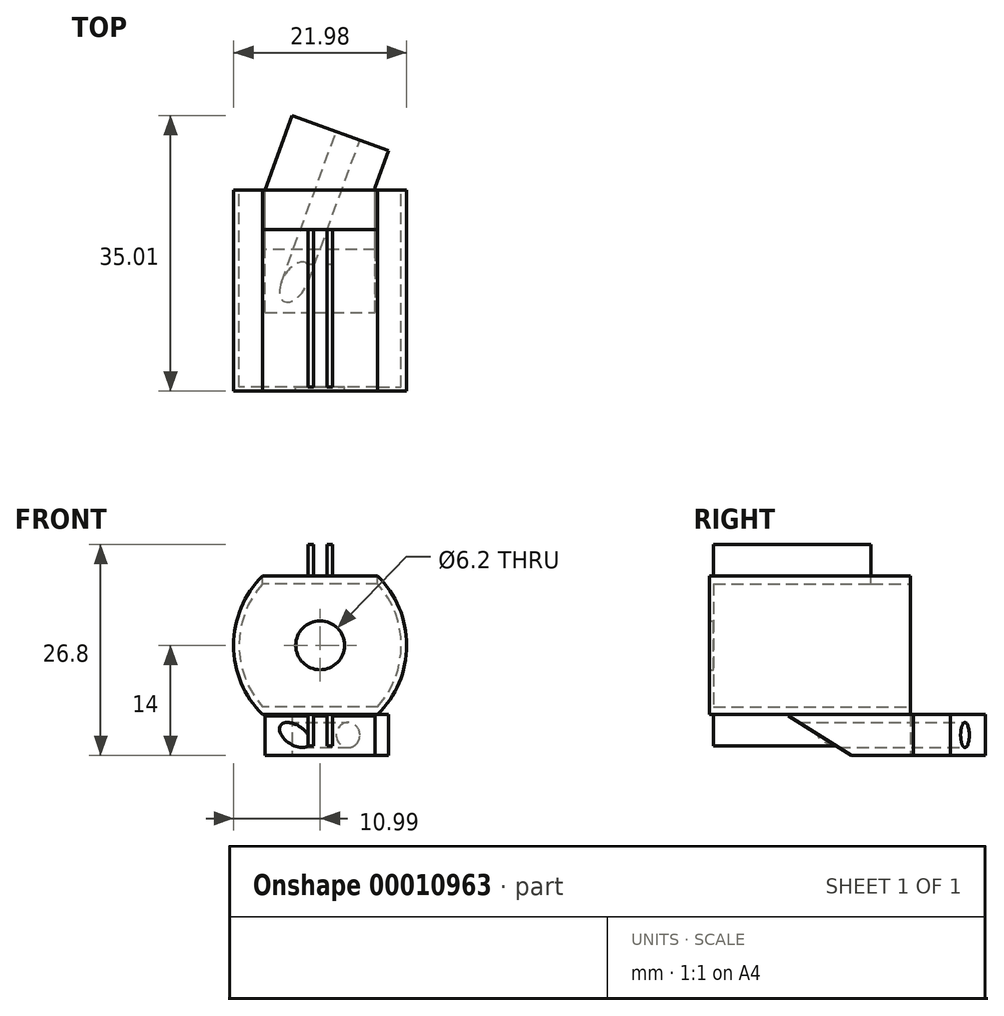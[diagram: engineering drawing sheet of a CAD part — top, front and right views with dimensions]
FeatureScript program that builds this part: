
annotation { "Feature Type Name" : "Feature", "Feature Type Description" : "" }
export const myFeature = defineFeature(function(context is Context, id is Id, definition is map)
    precondition{}
    {
        {
            var Q0;
            Q0=qCreatedBy(makeId("Front.planeOp"),FACE);
            var sketch = newSketch(context, id + "F0", { "sketchPlane" : qUnion([Q0])});
            skLineSegment(sketch, "E0.bottom", {"start": v(8.64, -7.8) * mm, "end": v(-5.96, -7.8) * mm});
            skLineSegment(sketch, "E0.top", {"start": v(8.64, 7.8) * mm, "end": v(-5.96, 7.8) * mm});
            skLineSegment(sketch, "E0.left", {"start": v(8.64, -7.8) * mm, "end": v(8.64, 7.8) * mm, "construction": true});
            skLineSegment(sketch, "E0.right", {"start": v(-5.96, -7.8) * mm, "end": v(-5.96, 7.8) * mm, "construction": true});
            skLineSegment(sketch, "E1", {"start": v(-5.96, 0) * mm, "end": v(8.64, 0) * mm, "construction": true});
            skArc(sketch, "E2", {"start": v(-5.96, 7.8) * mm, "mid": v(-8.96, 0) * mm, "end": v(-5.96, -7.8) * mm});
            skArc(sketch, "E3", {"start": v(8.64, -7.8) * mm, "mid": v(11.64, 0) * mm, "end": v(8.64, 7.8) * mm});
            skLineSegment(sketch, "E4.bottom", {"start": v(-8.96, 8.8) * mm, "end": v(11.64, 8.8) * mm, "construction": true});
            skLineSegment(sketch, "E4.top", {"start": v(-8.96, -8.8) * mm, "end": v(11.64, -8.8) * mm, "construction": true});
            skLineSegment(sketch, "E4.left", {"start": v(-8.96, 8.8) * mm, "end": v(-8.96, -8.8) * mm, "construction": true});
            skLineSegment(sketch, "E4.right", {"start": v(11.64, 8.8) * mm, "end": v(11.64, -8.8) * mm, "construction": true});
            skLineSegment(sketch, "E5", {"start": v(-5.96, 0) * mm, "end": v(-8.96, 0) * mm, "construction": true});
            skLineSegment(sketch, "E6", {"start": v(8.64, 0) * mm, "end": v(11.64, 0) * mm, "construction": true});
            skLineSegment(sketch, "E7", {"start": v(1.34, 7.8) * mm, "end": v(1.34, 8.8) * mm, "construction": true});
            skLineSegment(sketch, "E8", {"start": v(1.34, -7.8) * mm, "end": v(1.34, -8.8) * mm, "construction": true});
            skLineSegment(sketch, "E9", {"start": v(-5.96, 8.8) * mm, "end": v(-8.96, 8.8) * mm, "construction": true});
            skLineSegment(sketch, "E10", {"start": v(-8.96, -8.8) * mm, "end": v(-5.96, -8.8) * mm, "construction": true});
            skLineSegment(sketch, "E11", {"start": v(8.64, 8.8) * mm, "end": v(11.64, 8.8) * mm, "construction": true});
            skLineSegment(sketch, "E12", {"start": v(11.64, -8.8) * mm, "end": v(8.64, -8.8) * mm, "construction": true});
            skArc(sketch, "E13", {"start": v(-5.96, 8.8) * mm, "mid": v(-9.65, 0) * mm, "end": v(-5.96, -8.8) * mm});
            skArc(sketch, "E14", {"start": v(8.64, -8.8) * mm, "mid": v(12.33, 0) * mm, "end": v(8.64, 8.8) * mm});
            skLineSegment(sketch, "E15", {"start": v(-5.96, 8.8) * mm, "end": v(-0.2, 8.8) * mm});
            skLineSegment(sketch, "E16", {"start": v(-5.96, -8.8) * mm, "end": v(8.64, -8.8) * mm});
            skLineSegment(sketch, "E17.bottom", {"start": v(2.9, 12.8) * mm, "end": v(2.2, 12.8) * mm});
            skLineSegment(sketch, "E17.top", {"start": v(2.9, 8.8) * mm, "end": v(2.2, 8.8) * mm, "construction": true});
            skLineSegment(sketch, "E17.left", {"start": v(2.9, 12.8) * mm, "end": v(2.9, 8.8) * mm});
            skLineSegment(sketch, "E17.right", {"start": v(2.2, 12.8) * mm, "end": v(2.2, 8.8) * mm});
            skLineSegment(sketch, "E18.bottom", {"start": v(0.5, 12.8) * mm, "end": v(-0.2, 12.8) * mm});
            skLineSegment(sketch, "E18.top", {"start": v(0.5, 8.8) * mm, "end": v(-0.2, 8.8) * mm, "construction": true});
            skLineSegment(sketch, "E18.left", {"start": v(0.5, 12.8) * mm, "end": v(0.5, 8.8) * mm});
            skLineSegment(sketch, "E18.right", {"start": v(-0.2, 12.8) * mm, "end": v(-0.2, 8.8) * mm});
            skLineSegment(sketch, "E19", {"start": v(0.5, 10.8) * mm, "end": v(2.2, 10.8) * mm, "construction": true});
            skPoint(sketch, "E19.endSnap0", {"position": v(2.2, 10.8) * mm});
            skLineSegment(sketch, "E20", {"start": v(1.34, 10.8) * mm, "end": v(1.34, 8.8) * mm, "construction": true});
            skLineSegment(sketch, "E21.trimOffspring", {"start": v(0.5, 8.8) * mm, "end": v(2.2, 8.8) * mm});
            skLineSegment(sketch, "E22.trimOffspring", {"start": v(2.9, 8.8) * mm, "end": v(8.64, 8.8) * mm});
            skLineSegment(sketch, "E23.MirrorCS", {"start": v(2.9, -12.8) * mm, "end": v(2.2, -12.8) * mm});
            skLineSegment(sketch, "E24.MirrorCS", {"start": v(2.2, -12.8) * mm, "end": v(2.2, -8.8) * mm});
            skLineSegment(sketch, "E25.MirrorCS", {"start": v(0.5, -12.8) * mm, "end": v(-0.2, -12.8) * mm});
            skLineSegment(sketch, "E26.MirrorCS", {"start": v(0.5, -12.8) * mm, "end": v(0.5, -8.8) * mm});
            skLineSegment(sketch, "E27.MirrorCS", {"start": v(1.34, -10.8) * mm, "end": v(1.34, -8.8) * mm, "construction": true});
            skLineSegment(sketch, "E28.MirrorCS", {"start": v(-0.2, -12.8) * mm, "end": v(-0.2, -8.8) * mm});
            skLineSegment(sketch, "E29.MirrorCS", {"start": v(0.5, -10.8) * mm, "end": v(2.2, -10.8) * mm, "construction": true});
            skPoint(sketch, "E30.MirrorP", {"position": v(2.2, -10.8) * mm});
            skLineSegment(sketch, "E31.MirrorCS", {"start": v(2.9, -12.8) * mm, "end": v(2.9, -8.8) * mm});
            skSolve(sketch);
        }
        {
            var Q0;
            Q0 = qSketchRegion(id + "F0", true);
            extrude(context, id + "F1", {"entities" : qUnion([Q0]), "depth" : 25 * mm});
        }
        {
            var Q0;
            Q0=makeQuery(id+"F1.opExtrude","CAP_FACE",FACE,{"disambiguationData":[OSD([sQuery(id+"F0.wireOp",EDGE,"E0.bottom"),sQuery(id+"F0.wireOp",EDGE,"E0.top"),sQuery(id+"F0.wireOp",EDGE,"E2"),sQuery(id+"F0.wireOp",EDGE,"E3"),sQuery(id+"F0.wireOp",EDGE,"E13"),sQuery(id+"F0.wireOp",EDGE,"E14"),sQuery(id+"F0.wireOp",EDGE,"E15"),sQuery(id+"F0.wireOp",EDGE,"E16"),sQuery(id+"F0.wireOp",EDGE,"b434bd08-9800-4ba8-86db-d2efdbc153f3.bottom"),sQuery(id+"F0.wireOp",EDGE,"b434bd08-9800-4ba8-86db-d2efdbc153f3.top"),sQuery(id+"F0.wireOp",EDGE,"b434bd08-9800-4ba8-86db-d2efdbc153f3.left"),sQuery(id+"F0.wireOp",EDGE,"b434bd08-9800-4ba8-86db-d2efdbc153f3.right"),sQuery(id+"F0.wireOp",EDGE,"e7ebadcb-095e-4845-b03f-53081afac3a3.left"),sQuery(id+"F0.wireOp",EDGE,"e7ebadcb-095e-4845-b03f-53081afac3a3.right"),sQuery(id+"F0.wireOp",EDGE,"705c6145-6b34-48c9-8387-370b78359147.trimOffspring"),sQuery(id+"F0.wireOp",EDGE,"64f156d2-0356-4655-a443-7f1b8c19d74f0.MirrorCS"),sQuery(id+"F0.wireOp",EDGE,"0e9b9350-3440-4c2f-b366-a9727cc7379a0.MirrorCS"),sQuery(id+"F0.wireOp",EDGE,"648d7584-0f17-4bc0-a4b6-e825e98bb7620.MirrorCS"),sQuery(id+"F0.wireOp",EDGE,"4065b29f-1cc0-427a-abbd-1765cdf15fe30.MirrorCS"),sQuery(id+"F0.wireOp",EDGE,"a082fcf7-8d46-4496-8694-aedf1b6aa8e40.MirrorCS"),sQuery(id+"F0.wireOp",EDGE,"b75a4674-45b7-4ab3-ad6c-8b33a67d18960.MirrorCS")])],"isStart":true});
            var sketch = newSketch(context, id + "F2", { "sketchPlane" : qUnion([Q0])});
            skLineSegment(sketch, "E32.bottom", {"start": v(5.96, 7.8) * mm, "end": v(-8.64, 7.8) * mm});
            skLineSegment(sketch, "E32.top", {"start": v(5.96, 18.17) * mm, "end": v(-8.64, 18.17) * mm});
            skLineSegment(sketch, "E32.left", {"start": v(5.96, 7.8) * mm, "end": v(5.96, 18.17) * mm});
            skLineSegment(sketch, "E32.right", {"start": v(-8.64, 7.8) * mm, "end": v(-8.64, 18.17) * mm});
            skSolve(sketch);
        }
        {
            var Q0;
            Q0 = qSketchRegion(id + "F2", true);
            extrude(context, id + "F3", {"entities" : qUnion([Q0]), "operationType" : NewBodyOperationType.REMOVE, "oppositeDirection" : true, "depth" : 5 * mm});
        }
        {
            var Q0;
            Q0=makeQuery(id+"F1.opExtrude","CAP_FACE",FACE,{"disambiguationData":[OSD([sQuery(id+"F0.wireOp",EDGE,"E0.bottom"),sQuery(id+"F0.wireOp",EDGE,"E0.top"),sQuery(id+"F0.wireOp",EDGE,"E2"),sQuery(id+"F0.wireOp",EDGE,"E3"),sQuery(id+"F0.wireOp",EDGE,"E13"),sQuery(id+"F0.wireOp",EDGE,"E14"),sQuery(id+"F0.wireOp",EDGE,"E15"),sQuery(id+"F0.wireOp",EDGE,"E16"),sQuery(id+"F0.wireOp",EDGE,"b434bd08-9800-4ba8-86db-d2efdbc153f3.bottom"),sQuery(id+"F0.wireOp",EDGE,"b434bd08-9800-4ba8-86db-d2efdbc153f3.top"),sQuery(id+"F0.wireOp",EDGE,"b434bd08-9800-4ba8-86db-d2efdbc153f3.left"),sQuery(id+"F0.wireOp",EDGE,"b434bd08-9800-4ba8-86db-d2efdbc153f3.right"),sQuery(id+"F0.wireOp",EDGE,"e7ebadcb-095e-4845-b03f-53081afac3a3.left"),sQuery(id+"F0.wireOp",EDGE,"e7ebadcb-095e-4845-b03f-53081afac3a3.right"),sQuery(id+"F0.wireOp",EDGE,"705c6145-6b34-48c9-8387-370b78359147.trimOffspring"),sQuery(id+"F0.wireOp",EDGE,"64f156d2-0356-4655-a443-7f1b8c19d74f0.MirrorCS"),sQuery(id+"F0.wireOp",EDGE,"0e9b9350-3440-4c2f-b366-a9727cc7379a0.MirrorCS"),sQuery(id+"F0.wireOp",EDGE,"648d7584-0f17-4bc0-a4b6-e825e98bb7620.MirrorCS"),sQuery(id+"F0.wireOp",EDGE,"4065b29f-1cc0-427a-abbd-1765cdf15fe30.MirrorCS"),sQuery(id+"F0.wireOp",EDGE,"a082fcf7-8d46-4496-8694-aedf1b6aa8e40.MirrorCS"),sQuery(id+"F0.wireOp",EDGE,"b75a4674-45b7-4ab3-ad6c-8b33a67d18960.MirrorCS")])],"isStart":false});
            var sketch = newSketch(context, id + "F4", { "sketchPlane" : qUnion([Q0])});
            skArc(sketch, "E33.0", {"start": v(-5.96, 8.8) * mm, "mid": v(-9.65, 0) * mm, "end": v(-5.96, -8.8) * mm});
            skArc(sketch, "E34.0", {"start": v(8.64, -8.8) * mm, "mid": v(12.33, 0) * mm, "end": v(8.64, 8.8) * mm});
            skLineSegment(sketch, "E35", {"start": v(-5.96, 8.8) * mm, "end": v(8.64, 8.8) * mm});
            skLineSegment(sketch, "E36", {"start": v(8.64, -8.8) * mm, "end": v(-5.96, -8.8) * mm});
            skLineSegment(sketch, "E37", {"start": v(1.34, 8.8) * mm, "end": v(1.34, 0) * mm, "construction": true});
            skLineSegment(sketch, "E38", {"start": v(1.34, 0) * mm, "end": v(1.34, -8.8) * mm, "construction": true});
            skCircle(sketch, "E39", {"center": v(1.34, 0) * mm, "radius": 3.1 * mm});
            skSolve(sketch);
        }
        {
            var Q0;
            Q0 = qSketchRegion(id + "F4", true);
            extrude(context, id + "F5", {"entities" : qUnion([Q0]), "operationType" : NewBodyOperationType.ADD, "depth" : 0.5 * mm});
        }
        {
            var Q0;
            Q0=qCreatedBy(makeId("Top.planeOp"),FACE);
            cPlane(context, id + "F6", {"entities" : qUnion([Q0]), "cplaneType" : CPlaneType.OFFSET, "offset" : 14 * mm, "oppositeDirection" : true, "width" : 150 * mm, "height" : 150 * mm});
        }
        {
            var Q0;
            Q0=qCreatedBy(id+"F6.planeOp",FACE);
            var sketch = newSketch(context, id + "F7", { "sketchPlane" : qUnion([Q0])});
            skLineSegment(sketch, "E40.bottom", {"start": v(-5.66, -15.5) * mm, "end": v(8.34, -15.5) * mm});
            skLineSegment(sketch, "E40.top", {"start": v(-5.66, 0) * mm, "end": v(8.34, 0) * mm});
            skLineSegment(sketch, "E40.left", {"start": v(-5.66, -15.5) * mm, "end": v(-5.66, 0) * mm});
            skLineSegment(sketch, "E40.right", {"start": v(8.34, -15.5) * mm, "end": v(8.34, 0) * mm});
            skLineSegment(sketch, "E41", {"start": v(0.5, -25) * mm, "end": v(2.2, -25) * mm, "construction": true});
            skLineSegment(sketch, "E42", {"start": v(1.34, -25) * mm, "end": v(1.34, -15.5) * mm, "construction": true});
            skSolve(sketch);
        }
        {
            var Q0;
            Q0 = qSketchRegion(id + "F7", true);
            var Q1;
            Q1=makeQuery(id+"F1.opExtrude","SWEPT_BODY",BODY,{"disambiguationData":[OSD([sQuery(id+"F0.wireOp",EDGE,"E0.bottom"),sQuery(id+"F0.wireOp",EDGE,"E0.top"),sQuery(id+"F0.wireOp",EDGE,"E2"),sQuery(id+"F0.wireOp",EDGE,"E3"),sQuery(id+"F0.wireOp",EDGE,"E13"),sQuery(id+"F0.wireOp",EDGE,"E14"),sQuery(id+"F0.wireOp",EDGE,"E15"),sQuery(id+"F0.wireOp",EDGE,"E16"),sQuery(id+"F0.wireOp",EDGE,"b434bd08-9800-4ba8-86db-d2efdbc153f3.bottom"),sQuery(id+"F0.wireOp",EDGE,"b434bd08-9800-4ba8-86db-d2efdbc153f3.top"),sQuery(id+"F0.wireOp",EDGE,"b434bd08-9800-4ba8-86db-d2efdbc153f3.left"),sQuery(id+"F0.wireOp",EDGE,"b434bd08-9800-4ba8-86db-d2efdbc153f3.right"),sQuery(id+"F0.wireOp",EDGE,"e7ebadcb-095e-4845-b03f-53081afac3a3.left"),sQuery(id+"F0.wireOp",EDGE,"e7ebadcb-095e-4845-b03f-53081afac3a3.right"),sQuery(id+"F0.wireOp",EDGE,"705c6145-6b34-48c9-8387-370b78359147.trimOffspring"),sQuery(id+"F0.wireOp",EDGE,"64f156d2-0356-4655-a443-7f1b8c19d74f0.MirrorCS"),sQuery(id+"F0.wireOp",EDGE,"0e9b9350-3440-4c2f-b366-a9727cc7379a0.MirrorCS"),sQuery(id+"F0.wireOp",EDGE,"648d7584-0f17-4bc0-a4b6-e825e98bb7620.MirrorCS"),sQuery(id+"F0.wireOp",EDGE,"4065b29f-1cc0-427a-abbd-1765cdf15fe30.MirrorCS"),sQuery(id+"F0.wireOp",EDGE,"a082fcf7-8d46-4496-8694-aedf1b6aa8e40.MirrorCS"),sQuery(id+"F0.wireOp",EDGE,"b75a4674-45b7-4ab3-ad6c-8b33a67d18960.MirrorCS")])]});
            extrude(context, id + "F8", {"entities" : qUnion([Q0]), "operationType" : NewBodyOperationType.ADD, "endBound" : BoundingType.UP_TO_BODY, "endBoundEntityBody" : qUnion([Q1]), "depth" : 25 * mm});
        }
        {
            var Q0;
            Q0=makeQuery(id+"F8.opExtrude","CAP_FACE",FACE,{"disambiguationData":[OSD([sQuery(id+"F7.wireOp",EDGE,"E40.bottom"),sQuery(id+"F7.wireOp",EDGE,"E40.top"),sQuery(id+"F7.wireOp",EDGE,"E40.left"),sQuery(id+"F7.wireOp",EDGE,"E40.right")])],"isStart":true});
            var sketch = newSketch(context, id + "F9", { "sketchPlane" : qUnion([Q0])});
            skLineSegment(sketch, "E43", {"start": v(-0.02, 0) * mm, "end": v(-5.66, 15.5) * mm, "construction": true});
            skSolve(sketch);
        }
        {
            var Q0;
            Q0=sQuery(id+"F9.wireOp",EDGE,"E43");
            var Q1;
            Q1=sQuery(id+"F9.wireOp",VERTEX,"E43.start");
            cPlane(context, id + "F10", {"entities" : qUnion([Q0, Q1]), "cplaneType" : CPlaneType.CURVE_POINT, "offset" : 150 * mm, "width" : 150 * mm, "height" : 150 * mm});
        }
        {
            var Q0;
            Q0=makeQuery(id+"F8.opExtrude","CAP_EDGE",EDGE,{"disambiguationData":[OSD([sQuery(id+"F7.wireOp",EDGE,"E40.bottom")])],"isStart":true});
            chamfer(context, id + "F11", {"entities" : qUnion([Q0]), "chamferType" : ChamferType.TWO_OFFSETS, "width1" : 5 * mm, "oppositeDirection" : false, "width2" : 8 * mm, "tangentPropagation" : true});
        }
        {
            var Q0;
            Q0=makeQuery(id+"F9.imprint","IMPRINT",FACE,{"disambiguationData":[TD([[makeQuery(id+"F9.imprint","IMPRINT",EDGE,{"derivedFrom":makeQuery(id+"F8.opExtrude","CAP_EDGE",EDGE,{"disambiguationData":[OSD([sQuery(id+"F7.wireOp",EDGE,"E40.bottom")])],"isStart":true})}),-1.0]])]});
            var sketch = newSketch(context, id + "F12", { "sketchPlane" : qUnion([Q0])});
            skLineSegment(sketch, "E44", {"start": v(8.34, -0.35) * mm, "end": v(-3.9, -4.8) * mm});
            skLineSegment(sketch, "E45", {"start": v(-5.66, 0) * mm, "end": v(8.34, 0) * mm});
            skLineSegment(sketch, "E46", {"start": v(8.34, -0.35) * mm, "end": v(8.34, 0) * mm});
            skLineSegment(sketch, "E47", {"start": v(-3.9, -4.8) * mm, "end": v(-5.66, 0) * mm});
            skSolve(sketch);
        }
        {
            var Q0;
            Q0 = qSketchRegion(id + "F12", true);
            var Q1;
            {var subQ0=sQuery(id+"F0.wireOp",EDGE,"E16");Q1=makeQuery(id+"F5.boolean.opBoolean","MERGE",FACE,{"derivedFrom":[makeQuery(id+"F1.opExtrude","SWEPT_FACE",FACE,{"disambiguationData":[OSD([subQ0]),TDD([makeQuery(id+"F0.imprint","IMPRINT",EDGE,{"disambiguationData":[TD([[makeQuery(id+"F0.imprint","INTERSECT",VERTEX,{"derivedFrom":[sQuery(id+"F0.wireOp",EDGE,"E13"),subQ0]}),-1.0]])],"derivedFrom":subQ0})])]}),makeQuery(id+"F1.opExtrude","SWEPT_FACE",FACE,{"disambiguationData":[OSD([subQ0]),TDD([makeQuery(id+"F0.imprint","IMPRINT",EDGE,{"disambiguationData":[TD([[makeQuery(id+"F0.imprint","INTERSECT",VERTEX,{"derivedFrom":[subQ0,sQuery(id+"F0.wireOp",EDGE,"E24.MirrorCS")]}),1.0]])],"derivedFrom":subQ0})])]}),makeQuery(id+"F1.opExtrude","SWEPT_FACE",FACE,{"disambiguationData":[OSD([subQ0]),TDD([makeQuery(id+"F0.imprint","IMPRINT",EDGE,{"disambiguationData":[TD([[makeQuery(id+"F0.imprint","INTERSECT",VERTEX,{"derivedFrom":[sQuery(id+"F0.wireOp",EDGE,"E14"),subQ0]}),1.0]])],"derivedFrom":subQ0})])]}),makeQuery(id+"F5.opExtrude","SWEPT_FACE",FACE,{"disambiguationData":[OSD([sQuery(id+"F4.wireOp",EDGE,"E36")])]})]});}
            extrude(context, id + "F13", {"entities" : qUnion([Q0]), "operationType" : NewBodyOperationType.ADD, "endBound" : BoundingType.UP_TO_SURFACE, "oppositeDirection" : true, "endBoundEntityFace" : qUnion([Q1]), "depth" : 5.75 * mm});
        }
        {
            var Q0;
            Q0=qCreatedBy(id+"F10.planeOp",FACE);
            var sketch = newSketch(context, id + "F14", { "sketchPlane" : qUnion([Q0])});
            skCircle(sketch, "E48", {"center": v(2.22, -11.4) * mm, "radius": 1.6 * mm});
            skLineSegment(sketch, "E49", {"start": v(-5.32, -11.4) * mm, "end": v(7.72, -11.4) * mm, "construction": true});
            skSolve(sketch);
        }
        {
            var Q0;
            Q0 = qSketchRegion(id + "F14", true);
            extrude(context, id + "F15", {"entities" : qUnion([Q0]), "operationType" : NewBodyOperationType.REMOVE, "depth" : 25 * mm, "hasSecondDirection" : true, "secondDirectionOppositeDirection" : true, "secondDirectionDepth" : 25 * mm});
        }
        {
            var Q0;
            Q0=makeQuery(id+"F13.boolean.opBoolean","MERGE",FACE,{"derivedFrom":[makeQuery(id+"F8.opExtrude","CAP_FACE",FACE,{"disambiguationData":[OSD([sQuery(id+"F7.wireOp",EDGE,"E40.bottom"),sQuery(id+"F7.wireOp",EDGE,"E40.top"),sQuery(id+"F7.wireOp",EDGE,"E40.left"),sQuery(id+"F7.wireOp",EDGE,"E40.right")])],"isStart":true}),makeQuery(id+"F13.opExtrude","CAP_FACE",FACE,{"disambiguationData":[OSD([sQuery(id+"F12.wireOp",EDGE,"E44"),sQuery(id+"F12.wireOp",EDGE,"E45"),sQuery(id+"F12.wireOp",EDGE,"E46"),sQuery(id+"F12.wireOp",EDGE,"E47")])],"isStart":true})]});
            var sketch = newSketch(context, id + "F16", { "sketchPlane" : qUnion([Q0])});
            skLineSegment(sketch, "E50", {"start": v(3.15, -0.73) * mm, "end": v(-9.87, -5.47) * mm});
            skSolve(sketch);
        }
        {
            var Q0;
            Q0=sQuery(id+"F16.wireOp",EDGE,"E50");
            var Q1;
            Q1=sQuery(id+"F16.wireOp",VERTEX,"E50.end");
            cPlane(context, id + "F17", {"entities" : qUnion([Q0, Q1]), "cplaneType" : CPlaneType.CURVE_POINT, "offset" : 150 * mm, "width" : 150 * mm, "height" : 150 * mm});
        }
        {
            var Q0;
            Q0=makeQuery(id+"F1.opExtrude","SWEPT_BODY",BODY,{"disambiguationData":[OSD([sQuery(id+"F0.wireOp",EDGE,"E0.bottom"),sQuery(id+"F0.wireOp",EDGE,"E0.top"),sQuery(id+"F0.wireOp",EDGE,"E2"),sQuery(id+"F0.wireOp",EDGE,"E3"),sQuery(id+"F0.wireOp",EDGE,"E13"),sQuery(id+"F0.wireOp",EDGE,"E14"),sQuery(id+"F0.wireOp",EDGE,"E15"),sQuery(id+"F0.wireOp",EDGE,"E16"),sQuery(id+"F0.wireOp",EDGE,"E17.bottom"),sQuery(id+"F0.wireOp",EDGE,"E17.left"),sQuery(id+"F0.wireOp",EDGE,"E17.right"),sQuery(id+"F0.wireOp",EDGE,"E18.bottom"),sQuery(id+"F0.wireOp",EDGE,"E18.left"),sQuery(id+"F0.wireOp",EDGE,"E18.right"),sQuery(id+"F0.wireOp",EDGE,"E21.trimOffspring"),sQuery(id+"F0.wireOp",EDGE,"E22.trimOffspring"),sQuery(id+"F0.wireOp",EDGE,"E23.MirrorCS"),sQuery(id+"F0.wireOp",EDGE,"E24.MirrorCS"),sQuery(id+"F0.wireOp",EDGE,"E25.MirrorCS"),sQuery(id+"F0.wireOp",EDGE,"E26.MirrorCS"),sQuery(id+"F0.wireOp",EDGE,"E28.MirrorCS"),sQuery(id+"F0.wireOp",EDGE,"E31.MirrorCS")])]});
            var Q1;
            Q1=qCreatedBy(id+"F17.planeOp",FACE);
            mirror(context, id + "F18", {"entities" : qUnion([Q0]), "mirrorPlane" : qUnion([Q1])});
        }
        {
            var Q0;
            Q0=makeQuery(id+"F18.opPattern","COPY",BODY,{"derivedFrom":makeQuery(id+"F1.opExtrude","SWEPT_BODY",BODY,{"disambiguationData":[OSD([sQuery(id+"F0.wireOp",EDGE,"E0.bottom"),sQuery(id+"F0.wireOp",EDGE,"E0.top"),sQuery(id+"F0.wireOp",EDGE,"E2"),sQuery(id+"F0.wireOp",EDGE,"E3"),sQuery(id+"F0.wireOp",EDGE,"E13"),sQuery(id+"F0.wireOp",EDGE,"E14"),sQuery(id+"F0.wireOp",EDGE,"E15"),sQuery(id+"F0.wireOp",EDGE,"E16"),sQuery(id+"F0.wireOp",EDGE,"E17.bottom"),sQuery(id+"F0.wireOp",EDGE,"E17.left"),sQuery(id+"F0.wireOp",EDGE,"E17.right"),sQuery(id+"F0.wireOp",EDGE,"E18.bottom"),sQuery(id+"F0.wireOp",EDGE,"E18.left"),sQuery(id+"F0.wireOp",EDGE,"E18.right"),sQuery(id+"F0.wireOp",EDGE,"E21.trimOffspring"),sQuery(id+"F0.wireOp",EDGE,"E22.trimOffspring"),sQuery(id+"F0.wireOp",EDGE,"E23.MirrorCS"),sQuery(id+"F0.wireOp",EDGE,"E24.MirrorCS"),sQuery(id+"F0.wireOp",EDGE,"E25.MirrorCS"),sQuery(id+"F0.wireOp",EDGE,"E26.MirrorCS"),sQuery(id+"F0.wireOp",EDGE,"E28.MirrorCS"),sQuery(id+"F0.wireOp",EDGE,"E31.MirrorCS")])]}),"instanceName":"1"});
            deleteBodies(context, id + "F19", {"entities" : qUnion([Q0])});
        }
        {
            var Q0;
            Q0=makeQuery(id+"F13.opExtrude","SWEPT_FACE",FACE,{"disambiguationData":[OSD([sQuery(id+"F12.wireOp",EDGE,"E44")])]});
            var sketch = newSketch(context, id + "F20", { "sketchPlane" : qUnion([Q0])});
            skLineSegment(sketch, "E51.bottom", {"start": v(5.32, -14) * mm, "end": v(-7.72, -14) * mm});
            skLineSegment(sketch, "E51.top", {"start": v(5.32, -8.8) * mm, "end": v(-7.72, -8.8) * mm});
            skLineSegment(sketch, "E51.left", {"start": v(5.32, -14) * mm, "end": v(5.32, -8.8) * mm});
            skLineSegment(sketch, "E51.right", {"start": v(-7.72, -14) * mm, "end": v(-7.72, -8.8) * mm});
            skCircle(sketch, "E52", {"center": v(-2.22, -11.4) * mm, "radius": 1.6 * mm});
            skSolve(sketch);
        }
        {
            var Q0;
            Q0 = qSketchRegion(id + "F20", true);
            extrude(context, id + "F21", {"entities" : qUnion([Q0]), "operationType" : NewBodyOperationType.ADD, "depth" : 5 * mm});
        }
    });
